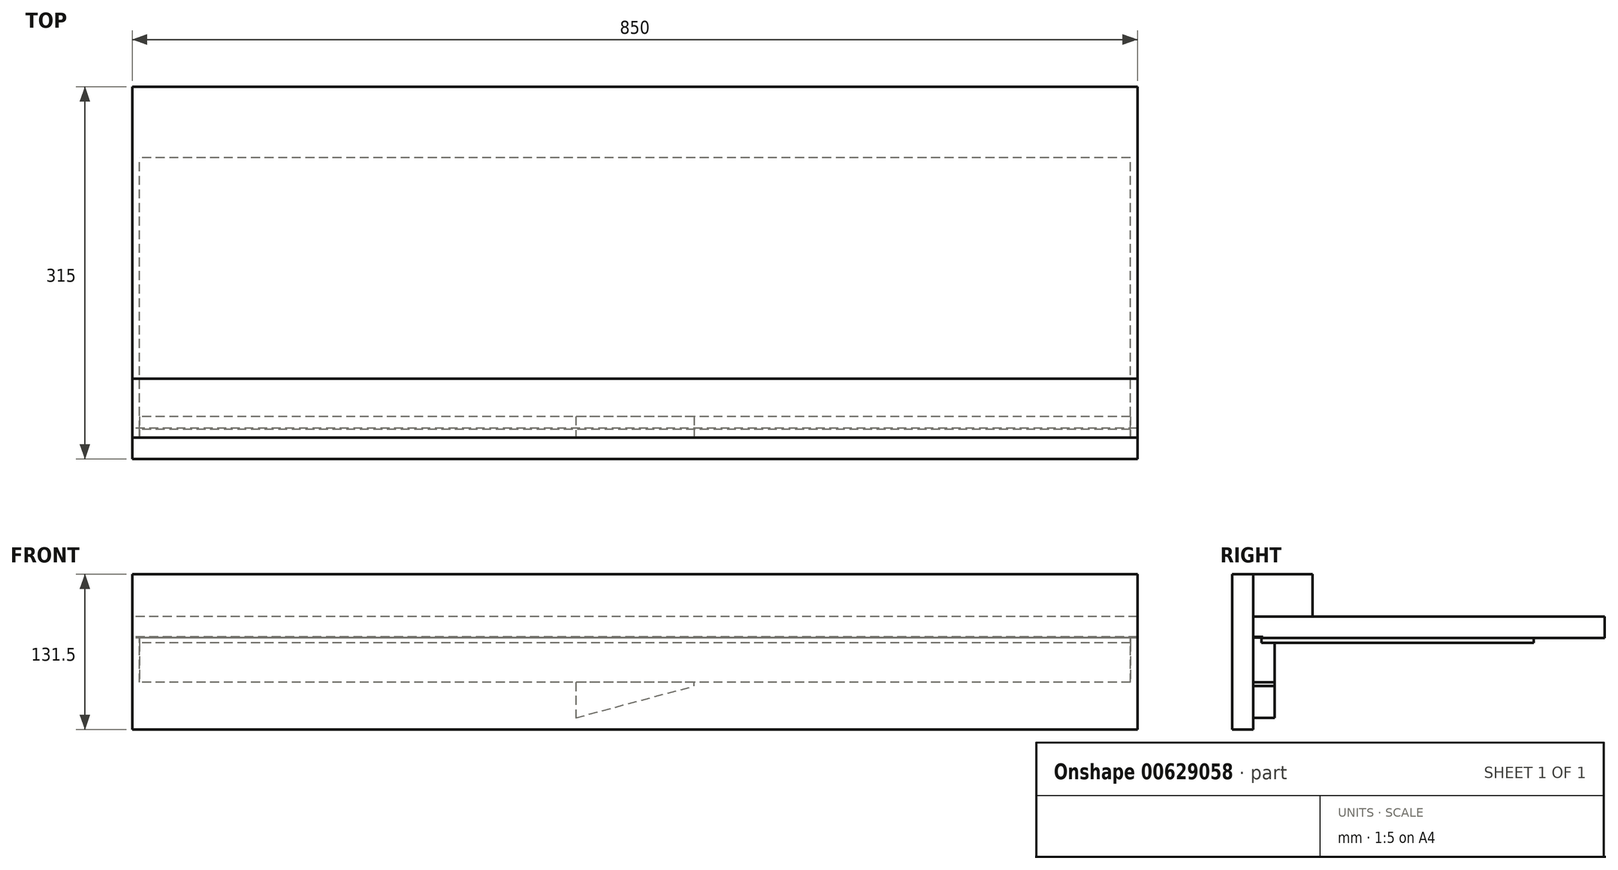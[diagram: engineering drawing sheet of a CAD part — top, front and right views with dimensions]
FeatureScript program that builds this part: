
annotation { "Feature Type Name" : "Feature", "Feature Type Description" : "" }
export const myFeature = defineFeature(function(context is Context, id is Id, definition is map)
    precondition{}
    {
        {
            var Q0;
            Q0=qCreatedBy(makeId("Right.planeOp"),FACE);
            var sketch = newSketch(context, id + "F0", { "sketchPlane" : qUnion([Q0])});
            skLineSegment(sketch, "E0.bottom", {"start": v(-11, 0) * mm, "end": v(219, 0) * mm});
            skLineSegment(sketch, "E0.top", {"start": v(-11, 4) * mm, "end": v(219, 4) * mm});
            skLineSegment(sketch, "E0.left", {"start": v(-11, 0) * mm, "end": v(-11, 4) * mm});
            skLineSegment(sketch, "E0.right", {"start": v(219, 0) * mm, "end": v(219, 4) * mm});
            skSolve(sketch);
        }
        {
            var Q0;
            Q0=qCreatedBy(makeId("Right.planeOp"),FACE);
            var sketch = newSketch(context, id + "F1", { "sketchPlane" : qUnion([Q0])});
            skLineSegment(sketch, "E1", {"start": v(-11, 4.5) * mm, "end": v(-11, 0) * mm});
            skLineSegment(sketch, "E2", {"start": v(-11, 0) * mm, "end": v(0, 0) * mm});
            skLineSegment(sketch, "E3", {"start": v(0, 0) * mm, "end": v(0, -33.5) * mm});
            skLineSegment(sketch, "E4", {"start": v(0, -33.5) * mm, "end": v(-18, -33.5) * mm});
            skLineSegment(sketch, "E5", {"start": v(-18, -33.5) * mm, "end": v(-18, 4.5) * mm});
            skLineSegment(sketch, "E6", {"start": v(-18, 4.5) * mm, "end": v(-11, 4.5) * mm});
            skSolve(sketch);
        }
        {
            var Q0;
            Q0=qCreatedBy(makeId("Right.planeOp"),FACE);
            var sketch = newSketch(context, id + "F2", { "sketchPlane" : qUnion([Q0])});
            skLineSegment(sketch, "E7.bottom", {"start": v(279, 4) * mm, "end": v(-10, 4) * mm});
            skLineSegment(sketch, "E7.top", {"start": v(279, 22) * mm, "end": v(-18, 22) * mm});
            skLineSegment(sketch, "E7.left", {"start": v(279, 4) * mm, "end": v(279, 22) * mm});
            skLineSegment(sketch, "E7.right", {"start": v(-18, 5) * mm, "end": v(-18, 22) * mm});
            skLineSegment(sketch, "E8", {"start": v(-18, 5) * mm, "end": v(-10, 5) * mm});
            skLineSegment(sketch, "E9", {"start": v(-10, 5) * mm, "end": v(-10, 4) * mm});
            skSolve(sketch);
        }
        {
            var Q0;
            Q0=qCreatedBy(makeId("Right.planeOp"),FACE);
            var sketch = newSketch(context, id + "F3", { "sketchPlane" : qUnion([Q0])});
            skLineSegment(sketch, "E10.bottom", {"start": v(-18, 22) * mm, "end": v(32, 22) * mm});
            skLineSegment(sketch, "E10.top", {"start": v(-18, 58) * mm, "end": v(32, 58) * mm});
            skLineSegment(sketch, "E10.left", {"start": v(-18, 22) * mm, "end": v(-18, 58) * mm});
            skLineSegment(sketch, "E10.right", {"start": v(32, 22) * mm, "end": v(32, 58) * mm});
            skSolve(sketch);
        }
        {
            var Q0;
            Q0=qCreatedBy(makeId("Right.planeOp"),FACE);
            var sketch = newSketch(context, id + "F4", { "sketchPlane" : qUnion([Q0])});
            skLineSegment(sketch, "E11.bottom", {"start": v(-18, 58) * mm, "end": v(-36, 58) * mm});
            skLineSegment(sketch, "E11.top", {"start": v(-18, -73.5) * mm, "end": v(-36, -73.5) * mm});
            skLineSegment(sketch, "E11.left", {"start": v(-18, 58) * mm, "end": v(-18, -73.5) * mm});
            skLineSegment(sketch, "E11.right", {"start": v(-36, 58) * mm, "end": v(-36, -73.5) * mm});
            skSolve(sketch);
        }
        {
            assignVariable(context, id + "F5", {"name" : "jigL", "anyValue" : 850});
        }
        {
            assignVariable(context, id + "F6", {"name" : "StepL", "anyValue" : 838});
        }
        {
            var Q0;
            Q0=makeQuery(id+"F2.imprint","IMPRINT",FACE,{"disambiguationData":[TD([[makeQuery(id+"F2.imprint","IMPRINT",EDGE,{"derivedFrom":sQuery(id+"F2.wireOp",EDGE,"E7.bottom")}),-1.0]])]});
            var Q1;
            Q1=makeQuery(id+"F3.imprint","IMPRINT",FACE,{"disambiguationData":[TD([[makeQuery(id+"F3.imprint","IMPRINT",EDGE,{"derivedFrom":sQuery(id+"F3.wireOp",EDGE,"E10.bottom")}),1.0]])]});
            var Q2;
            Q2=makeQuery(id+"F4.imprint","IMPRINT",FACE,{"disambiguationData":[TD([[makeQuery(id+"F4.imprint","IMPRINT",EDGE,{"derivedFrom":sQuery(id+"F4.wireOp",EDGE,"E11.bottom")}),1.0]])]});
            extrude(context, id + "F7", {"entities" : qUnion([Q0, Q1, Q2]), "endBound" : BoundingType.SYMMETRIC, "depth" : getVariable(context, 'jigL') * mm, "offsetDistance" : 25 * mm});
        }
        {
            var Q0;
            Q0=makeQuery(id+"F0.imprint","IMPRINT",FACE,{"disambiguationData":[TD([[makeQuery(id+"F0.imprint","IMPRINT",EDGE,{"derivedFrom":sQuery(id+"F0.wireOp",EDGE,"E0.bottom")}),1.0]])]});
            var Q1;
            Q1=makeQuery(id+"F1.imprint","IMPRINT",FACE,{"disambiguationData":[TD([[makeQuery(id+"F1.imprint","IMPRINT",EDGE,{"derivedFrom":sQuery(id+"F1.wireOp",EDGE,"E1")}),-1.0]])]});
            extrude(context, id + "F8", {"entities" : qUnion([Q0, Q1]), "endBound" : BoundingType.SYMMETRIC, "depth" : getVariable(context, 'StepL') * mm, "offsetDistance" : 25 * mm});
        }
        {
            var Q0;
            Q0=makeQuery(id+"F7.opExtrude","SWEPT_FACE",FACE,{"disambiguationData":[OSD([sQuery(id+"F4.wireOp",EDGE,"E11.left")])]});
            var sketch = newSketch(context, id + "F9", { "sketchPlane" : qUnion([Q0])});
            skLineSegment(sketch, "E12", {"start": v(-50, -33.5) * mm, "end": v(50, -33.5) * mm});
            skLineSegment(sketch, "E13", {"start": v(50, -33.5) * mm, "end": v(50, -63.5) * mm});
            skLineSegment(sketch, "E14", {"start": v(50, -63.5) * mm, "end": v(-50, -36.7) * mm});
            skLineSegment(sketch, "E15", {"start": v(-50, -36.7) * mm, "end": v(-50, -33.5) * mm});
            skSolve(sketch);
        }
        {
            var Q0;
            Q0=makeQuery(id+"F9.imprint","IMPRINT",FACE,{"disambiguationData":[TD([[makeQuery(id+"F9.imprint","IMPRINT",EDGE,{"derivedFrom":sQuery(id+"F9.wireOp",EDGE,"E12")}),-1.0]])]});
            extrude(context, id + "F10", {"entities" : qUnion([Q0]), "depth" : 18 * mm, "offsetDistance" : 25 * mm});
        }
    });
